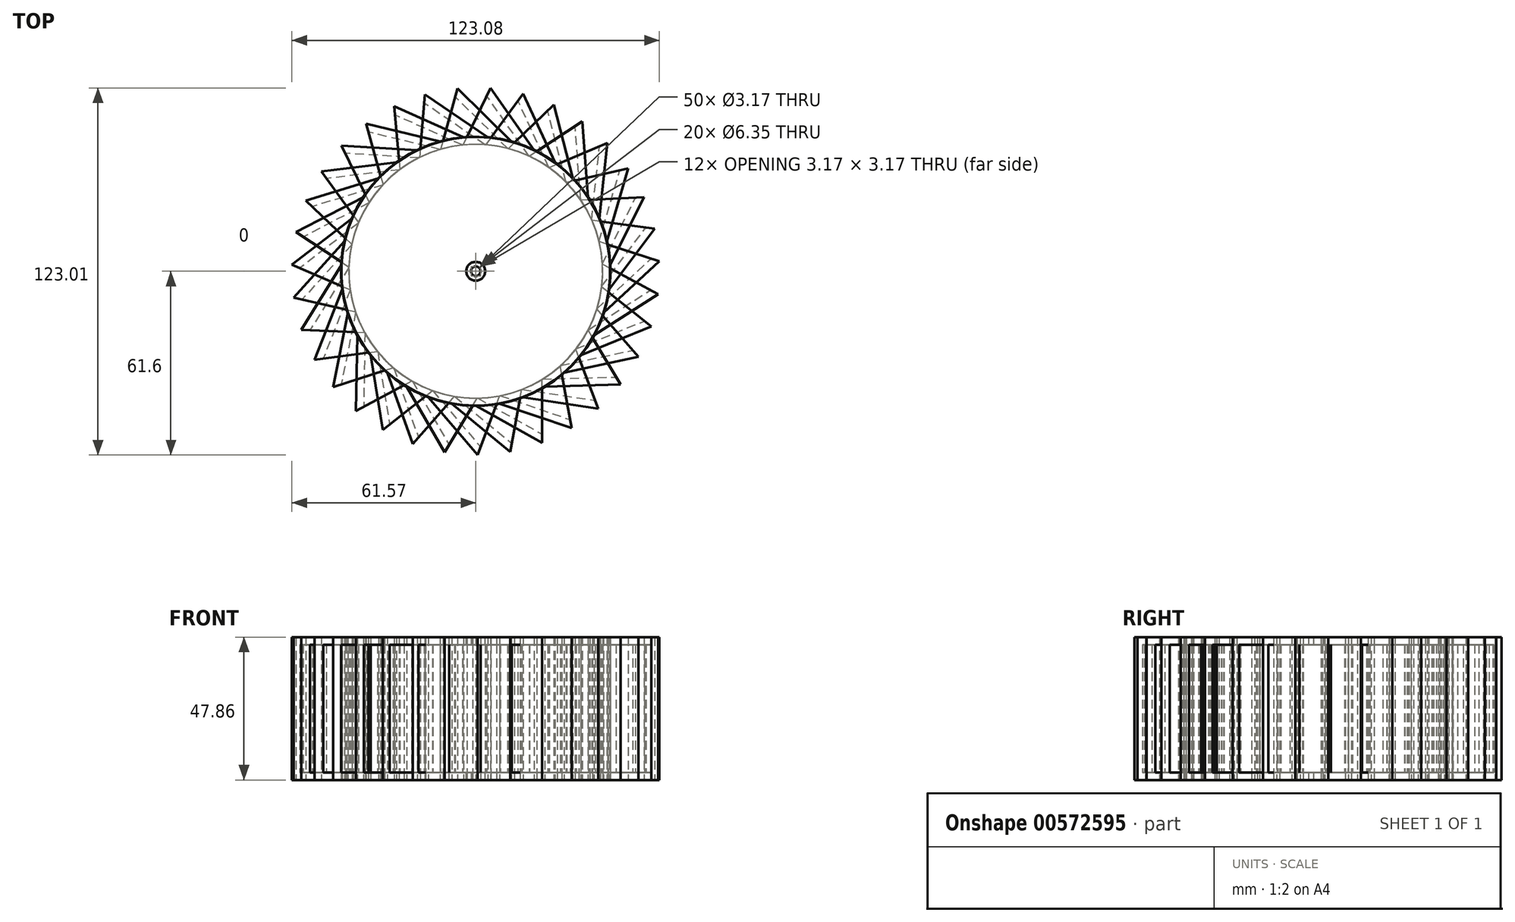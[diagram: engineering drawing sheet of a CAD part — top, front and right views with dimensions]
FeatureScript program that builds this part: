
annotation { "Feature Type Name" : "Feature", "Feature Type Description" : "" }
export const myFeature = defineFeature(function(context is Context, id is Id, definition is map)
    precondition{}
    {
        {
            var Q0;
            Q0=qCreatedBy(makeId("Top.planeOp"),FACE);
            var sketch = newSketch(context, id + "F0", { "sketchPlane" : qUnion([Q0])});
            skCircle(sketch, "E0", {"center": v(0, 0) * mm, "radius": 45.06 * mm});
            skLineSegment(sketch, "E1", {"start": v(0, -45.06) * mm, "end": v(22.2, -57.47) * mm});
            skLineSegment(sketch, "E2", {"start": v(22.2, -57.47) * mm, "end": v(22.2, -39.21) * mm});
            skSolve(sketch);
        }
        {
            var Q0;
            {var subQ0=sQuery(id+"F0.wireOp",EDGE,"E0");var subQ1=makeQuery(id+"F0.imprint","INTERSECT",VERTEX,{"derivedFrom":[subQ0,sQuery(id+"F0.wireOp",EDGE,"E1")]});Q0=makeQuery(id+"F0.imprint","IMPRINT",FACE,{"disambiguationData":[TD([[makeQuery(id+"F0.imprint","IMPRINT",EDGE,{"disambiguationData":[TD([[subQ1,-1.0]])],"derivedFrom":subQ0}),1.0]])]});}
            var Q1;
            {var subQ0=sQuery(id+"F0.wireOp",EDGE,"E1");Q1=makeQuery(id+"F0.imprint","IMPRINT",FACE,{"disambiguationData":[TD([[makeQuery(id+"F0.imprint","IMPRINT",EDGE,{"derivedFrom":subQ0}),1.0]])]});}
            extrude(context, id + "F1", {"entities" : qUnion([Q0, Q1]), "depth" : 47.86 * mm, "offsetDistance" : 25.4 * mm});
        }
        {
            var Q0;
            Q0=makeQuery(id+"F1.opExtrude","SWEPT_BODY",BODY,{"disambiguationData":[OSD([sQuery(id+"F0.wireOp",EDGE,"E0"),sQuery(id+"F0.wireOp",EDGE,"E1"),sQuery(id+"F0.wireOp",EDGE,"E2")])]});
            var Q1;
            Q1=makeQuery(id+"F1.opExtrude","CAP_EDGE",EDGE,{"disambiguationData":[OSD([sQuery(id+"F0.wireOp",EDGE,"E0")])],"isStart":true});
            circularPattern(context, id + "F2", {"entities" : qUnion([Q0]), "axis" : qUnion([Q1]), "angle" : 360 * degree, "instanceCount" : 35, "equalSpace" : true});
        }
        {
            var Q0;
            Q0=makeQuery(id+"F2.opPattern","COPY",FACE,{"derivedFrom":makeQuery(id+"F1.opExtrude","SWEPT_FACE",FACE,{"disambiguationData":[OSD([sQuery(id+"F0.wireOp",EDGE,"E2")])]}),"instanceName":"6"});
            var Q1;
            Q1=makeQuery(id+"F2.opPattern","COPY",FACE,{"derivedFrom":makeQuery(id+"F1.opExtrude","SWEPT_FACE",FACE,{"disambiguationData":[OSD([sQuery(id+"F0.wireOp",EDGE,"E2")])]}),"instanceName":"7"});
            var Q2;
            Q2=makeQuery(id+"F2.opPattern","COPY",FACE,{"derivedFrom":makeQuery(id+"F1.opExtrude","SWEPT_FACE",FACE,{"disambiguationData":[OSD([sQuery(id+"F0.wireOp",EDGE,"E2")])]}),"instanceName":"5"});
            var Q3;
            Q3=makeQuery(id+"F2.opPattern","COPY",FACE,{"derivedFrom":makeQuery(id+"F1.opExtrude","SWEPT_FACE",FACE,{"disambiguationData":[OSD([sQuery(id+"F0.wireOp",EDGE,"E2")])]}),"instanceName":"3"});
            var Q4;
            Q4=makeQuery(id+"F2.opPattern","COPY",FACE,{"derivedFrom":makeQuery(id+"F1.opExtrude","SWEPT_FACE",FACE,{"disambiguationData":[OSD([sQuery(id+"F0.wireOp",EDGE,"E2")])]}),"instanceName":"2"});
            var Q5;
            Q5=makeQuery(id+"F2.opPattern","COPY",FACE,{"derivedFrom":makeQuery(id+"F1.opExtrude","SWEPT_FACE",FACE,{"disambiguationData":[OSD([sQuery(id+"F0.wireOp",EDGE,"E2")])]}),"instanceName":"8"});
            var Q6;
            Q6=makeQuery(id+"F2.opPattern","COPY",FACE,{"derivedFrom":makeQuery(id+"F1.opExtrude","SWEPT_FACE",FACE,{"disambiguationData":[OSD([sQuery(id+"F0.wireOp",EDGE,"E2")])]}),"instanceName":"4"});
            var Q7;
            Q7=makeQuery(id+"F1.opExtrude","SWEPT_FACE",FACE,{"disambiguationData":[OSD([sQuery(id+"F0.wireOp",EDGE,"E2")])]});
            var Q8;
            Q8=makeQuery(id+"F2.opPattern","COPY",FACE,{"derivedFrom":makeQuery(id+"F1.opExtrude","SWEPT_FACE",FACE,{"disambiguationData":[OSD([sQuery(id+"F0.wireOp",EDGE,"E2")])]}),"instanceName":"9"});
            var Q9;
            Q9=makeQuery(id+"F2.opPattern","COPY",FACE,{"derivedFrom":makeQuery(id+"F1.opExtrude","SWEPT_FACE",FACE,{"disambiguationData":[OSD([sQuery(id+"F0.wireOp",EDGE,"E2")])]}),"instanceName":"1"});
            shell(context, id + "F3", {"entities" : qUnion([Q0, Q1, Q2, Q3, Q4, Q5, Q6, Q7, Q8, Q9]), "thickness" : 2.54 * mm});
        }
        {
            var Q0;
            Q0=makeQuery(id+"F2.opPattern","COPY",FACE,{"derivedFrom":makeQuery(id+"F1.opExtrude","CAP_FACE",FACE,{"disambiguationData":[OSD([sQuery(id+"F0.wireOp",EDGE,"E0"),sQuery(id+"F0.wireOp",EDGE,"E1"),sQuery(id+"F0.wireOp",EDGE,"E2")])],"isStart":false}),"instanceName":"7"});
            var sketch = newSketch(context, id + "F4", { "sketchPlane" : qUnion([Q0])});
            skPoint(sketch, "E3", {"position": v(0, 0) * mm});
            skSolve(sketch);
        }
        {
            var Q0;
            Q0=sQuery(id+"F4.wireOp",VERTEX,"E3");
            var Q1;
            Q1=makeQuery(id+"F1.opExtrude","SWEPT_BODY",BODY,{"disambiguationData":[OSD([sQuery(id+"F0.wireOp",EDGE,"E0"),sQuery(id+"F0.wireOp",EDGE,"E1"),sQuery(id+"F0.wireOp",EDGE,"E2")])]});
            var Q2;
            Q2=makeQuery(id+"F2.opPattern","COPY",BODY,{"derivedFrom":makeQuery(id+"F1.opExtrude","SWEPT_BODY",BODY,{"disambiguationData":[OSD([sQuery(id+"F0.wireOp",EDGE,"E0"),sQuery(id+"F0.wireOp",EDGE,"E1"),sQuery(id+"F0.wireOp",EDGE,"E2")])]}),"instanceName":"1"});
            var Q3;
            Q3=makeQuery(id+"F2.opPattern","COPY",BODY,{"derivedFrom":makeQuery(id+"F1.opExtrude","SWEPT_BODY",BODY,{"disambiguationData":[OSD([sQuery(id+"F0.wireOp",EDGE,"E0"),sQuery(id+"F0.wireOp",EDGE,"E1"),sQuery(id+"F0.wireOp",EDGE,"E2")])]}),"instanceName":"2"});
            var Q4;
            Q4=makeQuery(id+"F2.opPattern","COPY",BODY,{"derivedFrom":makeQuery(id+"F1.opExtrude","SWEPT_BODY",BODY,{"disambiguationData":[OSD([sQuery(id+"F0.wireOp",EDGE,"E0"),sQuery(id+"F0.wireOp",EDGE,"E1"),sQuery(id+"F0.wireOp",EDGE,"E2")])]}),"instanceName":"3"});
            var Q5;
            Q5=makeQuery(id+"F2.opPattern","COPY",BODY,{"derivedFrom":makeQuery(id+"F1.opExtrude","SWEPT_BODY",BODY,{"disambiguationData":[OSD([sQuery(id+"F0.wireOp",EDGE,"E0"),sQuery(id+"F0.wireOp",EDGE,"E1"),sQuery(id+"F0.wireOp",EDGE,"E2")])]}),"instanceName":"4"});
            var Q6;
            Q6=makeQuery(id+"F2.opPattern","COPY",BODY,{"derivedFrom":makeQuery(id+"F1.opExtrude","SWEPT_BODY",BODY,{"disambiguationData":[OSD([sQuery(id+"F0.wireOp",EDGE,"E0"),sQuery(id+"F0.wireOp",EDGE,"E1"),sQuery(id+"F0.wireOp",EDGE,"E2")])]}),"instanceName":"5"});
            var Q7;
            Q7=makeQuery(id+"F2.opPattern","COPY",BODY,{"derivedFrom":makeQuery(id+"F1.opExtrude","SWEPT_BODY",BODY,{"disambiguationData":[OSD([sQuery(id+"F0.wireOp",EDGE,"E0"),sQuery(id+"F0.wireOp",EDGE,"E1"),sQuery(id+"F0.wireOp",EDGE,"E2")])]}),"instanceName":"6"});
            var Q8;
            Q8=makeQuery(id+"F2.opPattern","COPY",BODY,{"derivedFrom":makeQuery(id+"F1.opExtrude","SWEPT_BODY",BODY,{"disambiguationData":[OSD([sQuery(id+"F0.wireOp",EDGE,"E0"),sQuery(id+"F0.wireOp",EDGE,"E1"),sQuery(id+"F0.wireOp",EDGE,"E2")])]}),"instanceName":"7"});
            var Q9;
            Q9=makeQuery(id+"F2.opPattern","COPY",BODY,{"derivedFrom":makeQuery(id+"F1.opExtrude","SWEPT_BODY",BODY,{"disambiguationData":[OSD([sQuery(id+"F0.wireOp",EDGE,"E0"),sQuery(id+"F0.wireOp",EDGE,"E1"),sQuery(id+"F0.wireOp",EDGE,"E2")])]}),"instanceName":"8"});
            var Q10;
            Q10=makeQuery(id+"F2.opPattern","COPY",BODY,{"derivedFrom":makeQuery(id+"F1.opExtrude","SWEPT_BODY",BODY,{"disambiguationData":[OSD([sQuery(id+"F0.wireOp",EDGE,"E0"),sQuery(id+"F0.wireOp",EDGE,"E1"),sQuery(id+"F0.wireOp",EDGE,"E2")])]}),"instanceName":"9"});
            hole(context, id + "F5", {"style" : HoleStyle.SIMPLE, "endStyle" : HoleEndStyle.THROUGH, "holeDiameter" : 6.35 * mm, "isTappedThrough" : true, "tappedDepth" : 12.7 * mm, "tapClearance" : 3, "locations" : qUnion([Q0]), "scope" : qUnion([Q1, Q2, Q3, Q4, Q5, Q6, Q7, Q8, Q9, Q10])});
        }
        {
            var Q0;
            Q0=makeQuery(id+"F2.opPattern","COPY",FACE,{"derivedFrom":makeQuery(id+"F1.opExtrude","SWEPT_FACE",FACE,{"disambiguationData":[OSD([sQuery(id+"F0.wireOp",EDGE,"E2")])]}),"instanceName":"17"});
            var Q1;
            Q1=makeQuery(id+"F2.opPattern","COPY",FACE,{"derivedFrom":makeQuery(id+"F1.opExtrude","SWEPT_FACE",FACE,{"disambiguationData":[OSD([sQuery(id+"F0.wireOp",EDGE,"E2")])]}),"instanceName":"24"});
            var Q2;
            Q2=makeQuery(id+"F2.opPattern","COPY",FACE,{"derivedFrom":makeQuery(id+"F1.opExtrude","SWEPT_FACE",FACE,{"disambiguationData":[OSD([sQuery(id+"F0.wireOp",EDGE,"E2")])]}),"instanceName":"22"});
            var Q3;
            Q3=makeQuery(id+"F2.opPattern","COPY",FACE,{"derivedFrom":makeQuery(id+"F1.opExtrude","SWEPT_FACE",FACE,{"disambiguationData":[OSD([sQuery(id+"F0.wireOp",EDGE,"E2")])]}),"instanceName":"32"});
            var Q4;
            Q4=makeQuery(id+"F2.opPattern","COPY",FACE,{"derivedFrom":makeQuery(id+"F1.opExtrude","SWEPT_FACE",FACE,{"disambiguationData":[OSD([sQuery(id+"F0.wireOp",EDGE,"E2")])]}),"instanceName":"27"});
            var Q5;
            Q5=makeQuery(id+"F2.opPattern","COPY",FACE,{"derivedFrom":makeQuery(id+"F1.opExtrude","SWEPT_FACE",FACE,{"disambiguationData":[OSD([sQuery(id+"F0.wireOp",EDGE,"E2")])]}),"instanceName":"33"});
            var Q6;
            Q6=makeQuery(id+"F2.opPattern","COPY",FACE,{"derivedFrom":makeQuery(id+"F1.opExtrude","SWEPT_FACE",FACE,{"disambiguationData":[OSD([sQuery(id+"F0.wireOp",EDGE,"E2")])]}),"instanceName":"20"});
            var Q7;
            Q7=makeQuery(id+"F2.opPattern","COPY",FACE,{"derivedFrom":makeQuery(id+"F1.opExtrude","SWEPT_FACE",FACE,{"disambiguationData":[OSD([sQuery(id+"F0.wireOp",EDGE,"E2")])]}),"instanceName":"28"});
            var Q8;
            Q8=makeQuery(id+"F2.opPattern","COPY",FACE,{"derivedFrom":makeQuery(id+"F1.opExtrude","SWEPT_FACE",FACE,{"disambiguationData":[OSD([sQuery(id+"F0.wireOp",EDGE,"E2")])]}),"instanceName":"31"});
            var Q9;
            Q9=makeQuery(id+"F2.opPattern","COPY",FACE,{"derivedFrom":makeQuery(id+"F1.opExtrude","SWEPT_FACE",FACE,{"disambiguationData":[OSD([sQuery(id+"F0.wireOp",EDGE,"E2")])]}),"instanceName":"14"});
            var Q10;
            Q10=makeQuery(id+"F2.opPattern","COPY",FACE,{"derivedFrom":makeQuery(id+"F1.opExtrude","SWEPT_FACE",FACE,{"disambiguationData":[OSD([sQuery(id+"F0.wireOp",EDGE,"E2")])]}),"instanceName":"23"});
            var Q11;
            Q11=makeQuery(id+"F2.opPattern","COPY",FACE,{"derivedFrom":makeQuery(id+"F1.opExtrude","SWEPT_FACE",FACE,{"disambiguationData":[OSD([sQuery(id+"F0.wireOp",EDGE,"E2")])]}),"instanceName":"19"});
            var Q12;
            Q12=makeQuery(id+"F2.opPattern","COPY",FACE,{"derivedFrom":makeQuery(id+"F1.opExtrude","SWEPT_FACE",FACE,{"disambiguationData":[OSD([sQuery(id+"F0.wireOp",EDGE,"E2")])]}),"instanceName":"29"});
            var Q13;
            Q13=makeQuery(id+"F2.opPattern","COPY",FACE,{"derivedFrom":makeQuery(id+"F1.opExtrude","SWEPT_FACE",FACE,{"disambiguationData":[OSD([sQuery(id+"F0.wireOp",EDGE,"E2")])]}),"instanceName":"34"});
            var Q14;
            Q14=makeQuery(id+"F2.opPattern","COPY",FACE,{"derivedFrom":makeQuery(id+"F1.opExtrude","SWEPT_FACE",FACE,{"disambiguationData":[OSD([sQuery(id+"F0.wireOp",EDGE,"E2")])]}),"instanceName":"13"});
            var Q15;
            Q15=makeQuery(id+"F2.opPattern","COPY",FACE,{"derivedFrom":makeQuery(id+"F1.opExtrude","SWEPT_FACE",FACE,{"disambiguationData":[OSD([sQuery(id+"F0.wireOp",EDGE,"E2")])]}),"instanceName":"21"});
            var Q16;
            Q16=makeQuery(id+"F2.opPattern","COPY",FACE,{"derivedFrom":makeQuery(id+"F1.opExtrude","SWEPT_FACE",FACE,{"disambiguationData":[OSD([sQuery(id+"F0.wireOp",EDGE,"E2")])]}),"instanceName":"12"});
            var Q17;
            Q17=makeQuery(id+"F2.opPattern","COPY",FACE,{"derivedFrom":makeQuery(id+"F1.opExtrude","SWEPT_FACE",FACE,{"disambiguationData":[OSD([sQuery(id+"F0.wireOp",EDGE,"E2")])]}),"instanceName":"16"});
            var Q18;
            Q18=makeQuery(id+"F2.opPattern","COPY",FACE,{"derivedFrom":makeQuery(id+"F1.opExtrude","SWEPT_FACE",FACE,{"disambiguationData":[OSD([sQuery(id+"F0.wireOp",EDGE,"E2")])]}),"instanceName":"15"});
            var Q19;
            Q19=makeQuery(id+"F2.opPattern","COPY",FACE,{"derivedFrom":makeQuery(id+"F1.opExtrude","SWEPT_FACE",FACE,{"disambiguationData":[OSD([sQuery(id+"F0.wireOp",EDGE,"E2")])]}),"instanceName":"18"});
            var Q20;
            Q20=makeQuery(id+"F2.opPattern","COPY",FACE,{"derivedFrom":makeQuery(id+"F1.opExtrude","SWEPT_FACE",FACE,{"disambiguationData":[OSD([sQuery(id+"F0.wireOp",EDGE,"E2")])]}),"instanceName":"30"});
            var Q21;
            Q21=makeQuery(id+"F2.opPattern","COPY",FACE,{"derivedFrom":makeQuery(id+"F1.opExtrude","SWEPT_FACE",FACE,{"disambiguationData":[OSD([sQuery(id+"F0.wireOp",EDGE,"E2")])]}),"instanceName":"11"});
            var Q22;
            Q22=makeQuery(id+"F2.opPattern","COPY",FACE,{"derivedFrom":makeQuery(id+"F1.opExtrude","SWEPT_FACE",FACE,{"disambiguationData":[OSD([sQuery(id+"F0.wireOp",EDGE,"E2")])]}),"instanceName":"10"});
            var Q23;
            Q23=makeQuery(id+"F2.opPattern","COPY",FACE,{"derivedFrom":makeQuery(id+"F1.opExtrude","SWEPT_FACE",FACE,{"disambiguationData":[OSD([sQuery(id+"F0.wireOp",EDGE,"E2")])]}),"instanceName":"25"});
            var Q24;
            Q24=makeQuery(id+"F2.opPattern","COPY",FACE,{"derivedFrom":makeQuery(id+"F1.opExtrude","SWEPT_FACE",FACE,{"disambiguationData":[OSD([sQuery(id+"F0.wireOp",EDGE,"E2")])]}),"instanceName":"26"});
            shell(context, id + "F6", {"entities" : qUnion([Q0, Q1, Q2, Q3, Q4, Q5, Q6, Q7, Q8, Q9, Q10, Q11, Q12, Q13, Q14, Q15, Q16, Q17, Q18, Q19, Q20, Q21, Q22, Q23, Q24]), "thickness" : 2.54 * mm});
        }
        {
            var Q0;
            Q0=makeQuery(id+"F2.opPattern","COPY",FACE,{"derivedFrom":makeQuery(id+"F1.opExtrude","CAP_FACE",FACE,{"disambiguationData":[OSD([sQuery(id+"F0.wireOp",EDGE,"E0"),sQuery(id+"F0.wireOp",EDGE,"E1"),sQuery(id+"F0.wireOp",EDGE,"E2")])],"isStart":true}),"instanceName":"12"});
            var sketch = newSketch(context, id + "F7", { "sketchPlane" : qUnion([Q0])});
            skPoint(sketch, "E4", {"position": v(0, 0) * mm});
            skSolve(sketch);
        }
        {
            var Q0;
            Q0=sQuery(id+"F7.wireOp",VERTEX,"E4");
            var Q1;
            Q1=makeQuery(id+"F2.opPattern","COPY",BODY,{"derivedFrom":makeQuery(id+"F1.opExtrude","SWEPT_BODY",BODY,{"disambiguationData":[OSD([sQuery(id+"F0.wireOp",EDGE,"E0"),sQuery(id+"F0.wireOp",EDGE,"E1"),sQuery(id+"F0.wireOp",EDGE,"E2")])]}),"instanceName":"10"});
            var Q2;
            Q2=makeQuery(id+"F2.opPattern","COPY",BODY,{"derivedFrom":makeQuery(id+"F1.opExtrude","SWEPT_BODY",BODY,{"disambiguationData":[OSD([sQuery(id+"F0.wireOp",EDGE,"E0"),sQuery(id+"F0.wireOp",EDGE,"E1"),sQuery(id+"F0.wireOp",EDGE,"E2")])]}),"instanceName":"11"});
            var Q3;
            Q3=makeQuery(id+"F2.opPattern","COPY",BODY,{"derivedFrom":makeQuery(id+"F1.opExtrude","SWEPT_BODY",BODY,{"disambiguationData":[OSD([sQuery(id+"F0.wireOp",EDGE,"E0"),sQuery(id+"F0.wireOp",EDGE,"E1"),sQuery(id+"F0.wireOp",EDGE,"E2")])]}),"instanceName":"12"});
            var Q4;
            Q4=makeQuery(id+"F2.opPattern","COPY",BODY,{"derivedFrom":makeQuery(id+"F1.opExtrude","SWEPT_BODY",BODY,{"disambiguationData":[OSD([sQuery(id+"F0.wireOp",EDGE,"E0"),sQuery(id+"F0.wireOp",EDGE,"E1"),sQuery(id+"F0.wireOp",EDGE,"E2")])]}),"instanceName":"13"});
            var Q5;
            Q5=makeQuery(id+"F2.opPattern","COPY",BODY,{"derivedFrom":makeQuery(id+"F1.opExtrude","SWEPT_BODY",BODY,{"disambiguationData":[OSD([sQuery(id+"F0.wireOp",EDGE,"E0"),sQuery(id+"F0.wireOp",EDGE,"E1"),sQuery(id+"F0.wireOp",EDGE,"E2")])]}),"instanceName":"14"});
            var Q6;
            Q6=makeQuery(id+"F2.opPattern","COPY",BODY,{"derivedFrom":makeQuery(id+"F1.opExtrude","SWEPT_BODY",BODY,{"disambiguationData":[OSD([sQuery(id+"F0.wireOp",EDGE,"E0"),sQuery(id+"F0.wireOp",EDGE,"E1"),sQuery(id+"F0.wireOp",EDGE,"E2")])]}),"instanceName":"15"});
            var Q7;
            Q7=makeQuery(id+"F2.opPattern","COPY",BODY,{"derivedFrom":makeQuery(id+"F1.opExtrude","SWEPT_BODY",BODY,{"disambiguationData":[OSD([sQuery(id+"F0.wireOp",EDGE,"E0"),sQuery(id+"F0.wireOp",EDGE,"E1"),sQuery(id+"F0.wireOp",EDGE,"E2")])]}),"instanceName":"16"});
            var Q8;
            Q8=makeQuery(id+"F2.opPattern","COPY",BODY,{"derivedFrom":makeQuery(id+"F1.opExtrude","SWEPT_BODY",BODY,{"disambiguationData":[OSD([sQuery(id+"F0.wireOp",EDGE,"E0"),sQuery(id+"F0.wireOp",EDGE,"E1"),sQuery(id+"F0.wireOp",EDGE,"E2")])]}),"instanceName":"17"});
            var Q9;
            Q9=makeQuery(id+"F2.opPattern","COPY",BODY,{"derivedFrom":makeQuery(id+"F1.opExtrude","SWEPT_BODY",BODY,{"disambiguationData":[OSD([sQuery(id+"F0.wireOp",EDGE,"E0"),sQuery(id+"F0.wireOp",EDGE,"E1"),sQuery(id+"F0.wireOp",EDGE,"E2")])]}),"instanceName":"18"});
            var Q10;
            Q10=makeQuery(id+"F2.opPattern","COPY",BODY,{"derivedFrom":makeQuery(id+"F1.opExtrude","SWEPT_BODY",BODY,{"disambiguationData":[OSD([sQuery(id+"F0.wireOp",EDGE,"E0"),sQuery(id+"F0.wireOp",EDGE,"E1"),sQuery(id+"F0.wireOp",EDGE,"E2")])]}),"instanceName":"19"});
            var Q11;
            Q11=makeQuery(id+"F2.opPattern","COPY",BODY,{"derivedFrom":makeQuery(id+"F1.opExtrude","SWEPT_BODY",BODY,{"disambiguationData":[OSD([sQuery(id+"F0.wireOp",EDGE,"E0"),sQuery(id+"F0.wireOp",EDGE,"E1"),sQuery(id+"F0.wireOp",EDGE,"E2")])]}),"instanceName":"20"});
            var Q12;
            Q12=makeQuery(id+"F2.opPattern","COPY",BODY,{"derivedFrom":makeQuery(id+"F1.opExtrude","SWEPT_BODY",BODY,{"disambiguationData":[OSD([sQuery(id+"F0.wireOp",EDGE,"E0"),sQuery(id+"F0.wireOp",EDGE,"E1"),sQuery(id+"F0.wireOp",EDGE,"E2")])]}),"instanceName":"21"});
            var Q13;
            Q13=makeQuery(id+"F2.opPattern","COPY",BODY,{"derivedFrom":makeQuery(id+"F1.opExtrude","SWEPT_BODY",BODY,{"disambiguationData":[OSD([sQuery(id+"F0.wireOp",EDGE,"E0"),sQuery(id+"F0.wireOp",EDGE,"E1"),sQuery(id+"F0.wireOp",EDGE,"E2")])]}),"instanceName":"22"});
            var Q14;
            Q14=makeQuery(id+"F2.opPattern","COPY",BODY,{"derivedFrom":makeQuery(id+"F1.opExtrude","SWEPT_BODY",BODY,{"disambiguationData":[OSD([sQuery(id+"F0.wireOp",EDGE,"E0"),sQuery(id+"F0.wireOp",EDGE,"E1"),sQuery(id+"F0.wireOp",EDGE,"E2")])]}),"instanceName":"23"});
            var Q15;
            Q15=makeQuery(id+"F2.opPattern","COPY",BODY,{"derivedFrom":makeQuery(id+"F1.opExtrude","SWEPT_BODY",BODY,{"disambiguationData":[OSD([sQuery(id+"F0.wireOp",EDGE,"E0"),sQuery(id+"F0.wireOp",EDGE,"E1"),sQuery(id+"F0.wireOp",EDGE,"E2")])]}),"instanceName":"24"});
            var Q16;
            Q16=makeQuery(id+"F2.opPattern","COPY",BODY,{"derivedFrom":makeQuery(id+"F1.opExtrude","SWEPT_BODY",BODY,{"disambiguationData":[OSD([sQuery(id+"F0.wireOp",EDGE,"E0"),sQuery(id+"F0.wireOp",EDGE,"E1"),sQuery(id+"F0.wireOp",EDGE,"E2")])]}),"instanceName":"25"});
            var Q17;
            Q17=makeQuery(id+"F2.opPattern","COPY",BODY,{"derivedFrom":makeQuery(id+"F1.opExtrude","SWEPT_BODY",BODY,{"disambiguationData":[OSD([sQuery(id+"F0.wireOp",EDGE,"E0"),sQuery(id+"F0.wireOp",EDGE,"E1"),sQuery(id+"F0.wireOp",EDGE,"E2")])]}),"instanceName":"26"});
            var Q18;
            Q18=makeQuery(id+"F2.opPattern","COPY",BODY,{"derivedFrom":makeQuery(id+"F1.opExtrude","SWEPT_BODY",BODY,{"disambiguationData":[OSD([sQuery(id+"F0.wireOp",EDGE,"E0"),sQuery(id+"F0.wireOp",EDGE,"E1"),sQuery(id+"F0.wireOp",EDGE,"E2")])]}),"instanceName":"27"});
            var Q19;
            Q19=makeQuery(id+"F2.opPattern","COPY",BODY,{"derivedFrom":makeQuery(id+"F1.opExtrude","SWEPT_BODY",BODY,{"disambiguationData":[OSD([sQuery(id+"F0.wireOp",EDGE,"E0"),sQuery(id+"F0.wireOp",EDGE,"E1"),sQuery(id+"F0.wireOp",EDGE,"E2")])]}),"instanceName":"28"});
            var Q20;
            Q20=makeQuery(id+"F2.opPattern","COPY",BODY,{"derivedFrom":makeQuery(id+"F1.opExtrude","SWEPT_BODY",BODY,{"disambiguationData":[OSD([sQuery(id+"F0.wireOp",EDGE,"E0"),sQuery(id+"F0.wireOp",EDGE,"E1"),sQuery(id+"F0.wireOp",EDGE,"E2")])]}),"instanceName":"29"});
            var Q21;
            Q21=makeQuery(id+"F2.opPattern","COPY",BODY,{"derivedFrom":makeQuery(id+"F1.opExtrude","SWEPT_BODY",BODY,{"disambiguationData":[OSD([sQuery(id+"F0.wireOp",EDGE,"E0"),sQuery(id+"F0.wireOp",EDGE,"E1"),sQuery(id+"F0.wireOp",EDGE,"E2")])]}),"instanceName":"30"});
            var Q22;
            Q22=makeQuery(id+"F2.opPattern","COPY",BODY,{"derivedFrom":makeQuery(id+"F1.opExtrude","SWEPT_BODY",BODY,{"disambiguationData":[OSD([sQuery(id+"F0.wireOp",EDGE,"E0"),sQuery(id+"F0.wireOp",EDGE,"E1"),sQuery(id+"F0.wireOp",EDGE,"E2")])]}),"instanceName":"31"});
            var Q23;
            Q23=makeQuery(id+"F2.opPattern","COPY",BODY,{"derivedFrom":makeQuery(id+"F1.opExtrude","SWEPT_BODY",BODY,{"disambiguationData":[OSD([sQuery(id+"F0.wireOp",EDGE,"E0"),sQuery(id+"F0.wireOp",EDGE,"E1"),sQuery(id+"F0.wireOp",EDGE,"E2")])]}),"instanceName":"32"});
            var Q24;
            Q24=makeQuery(id+"F2.opPattern","COPY",BODY,{"derivedFrom":makeQuery(id+"F1.opExtrude","SWEPT_BODY",BODY,{"disambiguationData":[OSD([sQuery(id+"F0.wireOp",EDGE,"E0"),sQuery(id+"F0.wireOp",EDGE,"E1"),sQuery(id+"F0.wireOp",EDGE,"E2")])]}),"instanceName":"33"});
            var Q25;
            Q25=makeQuery(id+"F2.opPattern","COPY",BODY,{"derivedFrom":makeQuery(id+"F1.opExtrude","SWEPT_BODY",BODY,{"disambiguationData":[OSD([sQuery(id+"F0.wireOp",EDGE,"E0"),sQuery(id+"F0.wireOp",EDGE,"E1"),sQuery(id+"F0.wireOp",EDGE,"E2")])]}),"instanceName":"34"});
            hole(context, id + "F8", {"style" : HoleStyle.SIMPLE, "endStyle" : HoleEndStyle.THROUGH, "holeDiameter" : 3.17 * mm, "majorDiameter" : 6.35 * mm, "isTappedThrough" : true, "tappedDepth" : 12.7 * mm, "tapClearance" : 3, "locations" : qUnion([Q0]), "scope" : qUnion([Q1, Q2, Q3, Q4, Q5, Q6, Q7, Q8, Q9, Q10, Q11, Q12, Q13, Q14, Q15, Q16, Q17, Q18, Q19, Q20, Q21, Q22, Q23, Q24, Q25])});
        }
    });
